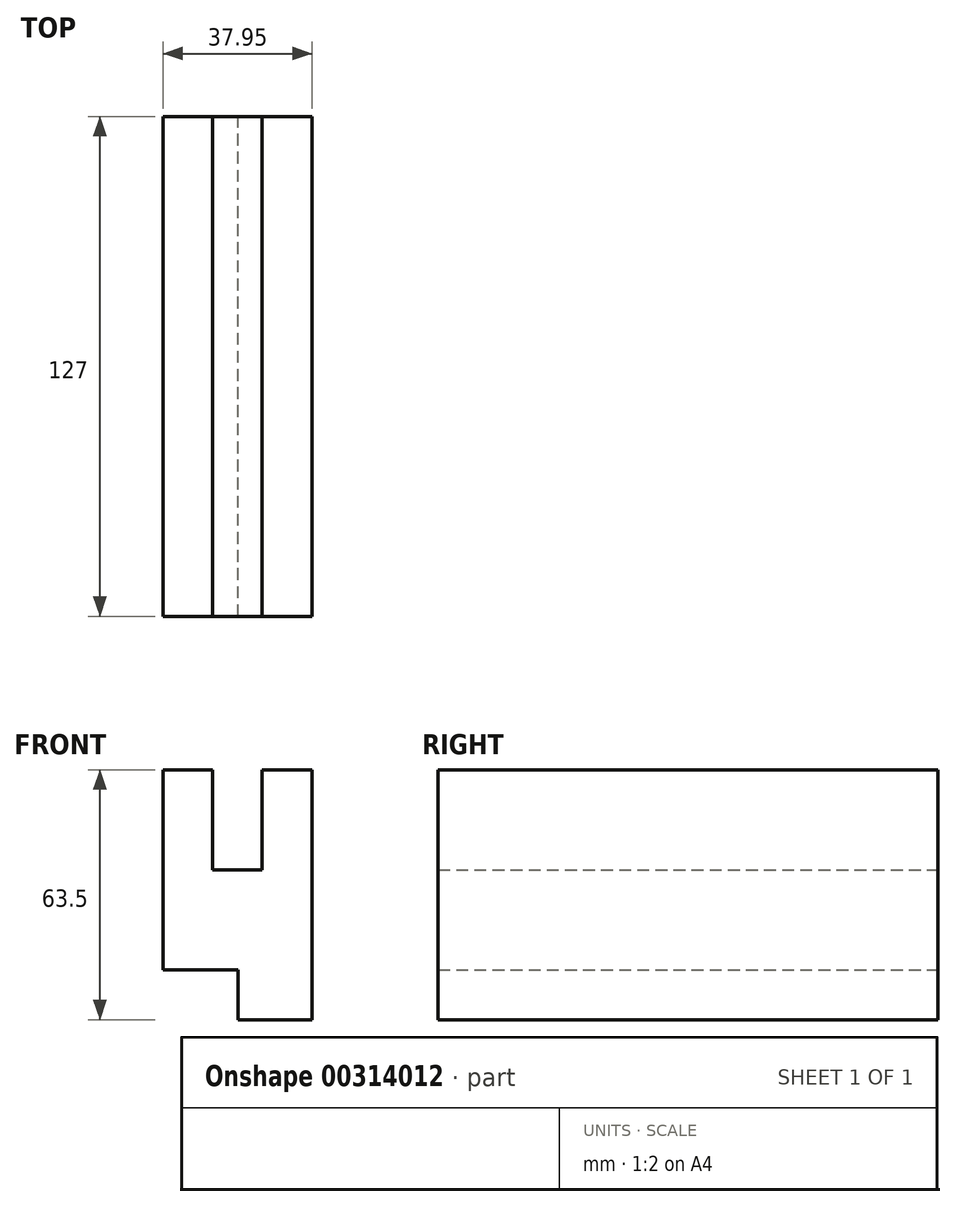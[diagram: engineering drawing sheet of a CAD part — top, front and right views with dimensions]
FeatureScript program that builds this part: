
annotation { "Feature Type Name" : "Feature", "Feature Type Description" : "" }
export const myFeature = defineFeature(function(context is Context, id is Id, definition is map)
    precondition{}
    {
        {
            var Q0;
            Q0=qCreatedBy(makeId("Front.planeOp"),FACE);
            var sketch = newSketch(context, id + "F0", { "sketchPlane" : qUnion([Q0])});
            skLineSegment(sketch, "E0", {"start": v(-36.87, 25.4) * mm, "end": v(-24.19, 25.4) * mm});
            skLineSegment(sketch, "E1", {"start": v(-36.87, 25.4) * mm, "end": v(-36.87, -25.4) * mm});
            skLineSegment(sketch, "E2", {"start": v(-36.87, -25.4) * mm, "end": v(-17.82, -25.4) * mm});
            skLineSegment(sketch, "E3", {"start": v(-17.82, -25.4) * mm, "end": v(-17.82, -38.1) * mm});
            skLineSegment(sketch, "E4", {"start": v(-17.82, -38.1) * mm, "end": v(1.08, -38.1) * mm});
            skLineSegment(sketch, "E5", {"start": v(1.08, -38.1) * mm, "end": v(1.08, 25.4) * mm});
            skLineSegment(sketch, "E6", {"start": v(1.08, 25.4) * mm, "end": v(-11.62, 25.4) * mm});
            skLineSegment(sketch, "E7", {"start": v(-11.62, 25.4) * mm, "end": v(-11.62, 0) * mm});
            skLineSegment(sketch, "E8", {"start": v(-24.19, 25.4) * mm, "end": v(-24.19, 0) * mm});
            skLineSegment(sketch, "E9", {"start": v(-24.19, 0) * mm, "end": v(-11.62, 0) * mm});
            skSolve(sketch);
        }
        {
            var Q0;
            Q0 = qSketchRegion(id + "F0", true);
            extrude(context, id + "F1", {"entities" : qUnion([Q0]), "depth" : 127 * mm});
        }
    });
